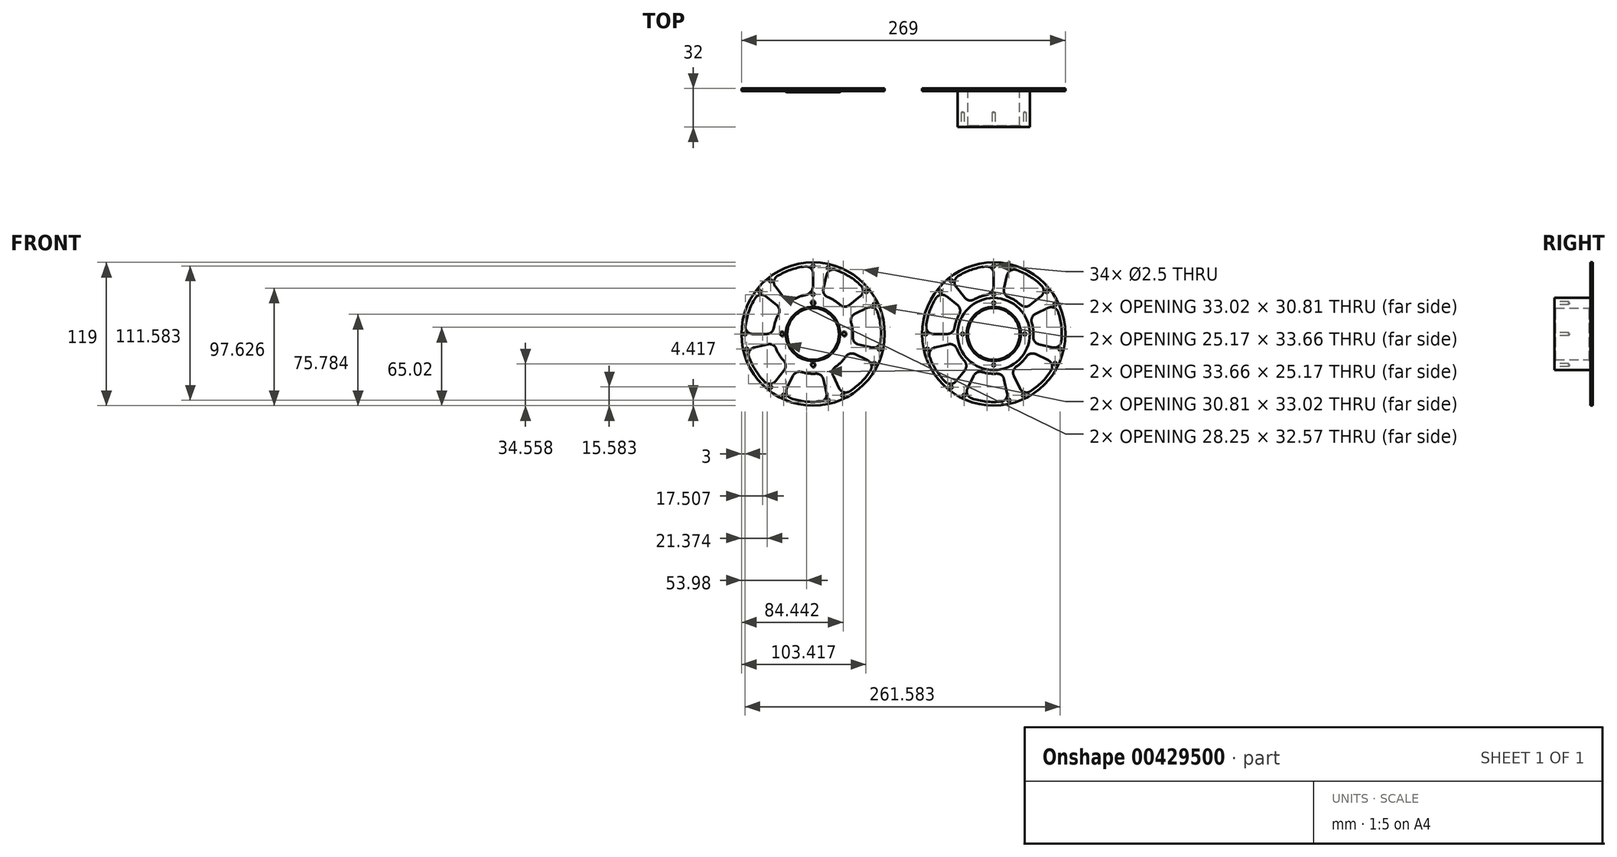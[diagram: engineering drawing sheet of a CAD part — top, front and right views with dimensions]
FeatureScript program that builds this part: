
annotation { "Feature Type Name" : "Feature", "Feature Type Description" : "" }
export const myFeature = defineFeature(function(context is Context, id is Id, definition is map)
    precondition{}
    {
        {
            var Q0;
            Q0=qCreatedBy(makeId("Front.planeOp"),FACE);
            var sketch = newSketch(context, id + "F0", { "sketchPlane" : qUnion([Q0])});
            skCircle(sketch, "E0", {"center": v(0, 0) * mm, "radius": 21.5 * mm});
            skCircle(sketch, "E1", {"center": v(0, 0) * mm, "radius": 30 * mm});
            skCircle(sketch, "E2", {"center": v(0, 0) * mm, "radius": 59.5 * mm});
            skArc(sketch, "E3", {"start": v(-6.44, 32.37) * mm, "mid": v(-11.55, 30.91) * mm, "end": v(-16.36, 28.66) * mm});
            skArc(sketch, "E4", {"start": v(-48.05, 29.73) * mm, "mid": v(-53.33, 18.66) * mm, "end": v(-56.1, 6.71) * mm});
            skLineSegment(sketch, "E5", {"start": v(0, 40.21) * mm, "end": v(0, 50.14) * mm});
            skLineSegment(sketch, "E6.1.0", {"start": v(-30.13, 24.03) * mm, "end": v(-39.2, 31.26) * mm});
            skLineSegment(sketch, "E6.2.0", {"start": v(-37.57, -8.57) * mm, "end": v(-48.89, -11.16) * mm});
            skLineSegment(sketch, "E6.3.0", {"start": v(-16.72, -34.72) * mm, "end": v(-21.76, -45.18) * mm});
            skLineSegment(sketch, "E6.4.0", {"start": v(16.72, -34.72) * mm, "end": v(21.76, -45.18) * mm});
            skLineSegment(sketch, "E6.5.0", {"start": v(37.57, -8.57) * mm, "end": v(48.89, -11.16) * mm});
            skLineSegment(sketch, "E7.1.6.0", {"start": v(30.13, 24.03) * mm, "end": v(39.2, 31.26) * mm});
            skLineSegment(sketch, "E8", {"start": v(-38.54, 0) * mm, "end": v(-50.14, 0) * mm});
            skLineSegment(sketch, "E9.1.0", {"start": v(-24.03, -30.13) * mm, "end": v(-31.26, -39.2) * mm});
            skLineSegment(sketch, "E9.2.0", {"start": v(8.57, -37.57) * mm, "end": v(11.16, -48.89) * mm});
            skLineSegment(sketch, "E9.3.0", {"start": v(34.72, -16.72) * mm, "end": v(45.18, -21.76) * mm});
            skLineSegment(sketch, "E9.4.0", {"start": v(34.72, 16.72) * mm, "end": v(45.18, 21.76) * mm});
            skLineSegment(sketch, "E9.5.0", {"start": v(8.57, 37.57) * mm, "end": v(11.16, 48.89) * mm});
            skLineSegment(sketch, "E9.6.0", {"start": v(-24.03, 30.13) * mm, "end": v(-31.26, 39.2) * mm});
            skArc(sketch, "E10.trimOffspring", {"start": v(-6.71, 56.1) * mm, "mid": v(-18.66, 53.33) * mm, "end": v(-29.73, 48.05) * mm});
            skArc(sketch, "E11.trimOffspring", {"start": v(-28.66, 16.36) * mm, "mid": v(-31.15, 10.9) * mm, "end": v(-32.6, 5.08) * mm});
            skArc(sketch, "E12.trimOffspring", {"start": v(-53.2, -19.03) * mm, "mid": v(-47.84, -30.06) * mm, "end": v(-40.23, -39.68) * mm});
            skArc(sketch, "E13.trimOffspring", {"start": v(-30.66, -12.2) * mm, "mid": v(-27.94, -17.56) * mm, "end": v(-24.3, -22.33) * mm});
            skArc(sketch, "E14.trimOffspring", {"start": v(-9.57, -31.58) * mm, "mid": v(-3.7, -32.8) * mm, "end": v(2.3, -32.92) * mm});
            skArc(sketch, "E15.trimOffspring", {"start": v(-18.3, -53.46) * mm, "mid": v(-6.33, -56.14) * mm, "end": v(5.94, -56.19) * mm});
            skArc(sketch, "E16.trimOffspring", {"start": v(18.72, -27.18) * mm, "mid": v(23.33, -23.33) * mm, "end": v(27.18, -18.72) * mm});
            skArc(sketch, "E17.trimOffspring", {"start": v(30.39, -47.63) * mm, "mid": v(39.95, -39.95) * mm, "end": v(47.63, -30.39) * mm});
            skArc(sketch, "E18.trimOffspring", {"start": v(32.92, -2.3) * mm, "mid": v(32.8, 3.7) * mm, "end": v(31.58, 9.57) * mm});
            skArc(sketch, "E19.trimOffspring", {"start": v(56.19, -5.94) * mm, "mid": v(56.14, 6.33) * mm, "end": v(53.46, 18.3) * mm});
            skArc(sketch, "E20.trimOffspring", {"start": v(39.68, 40.23) * mm, "mid": v(30.06, 47.84) * mm, "end": v(19.03, 53.2) * mm});
            skArc(sketch, "E21.trimOffspring", {"start": v(22.33, 24.3) * mm, "mid": v(17.56, 27.94) * mm, "end": v(12.2, 30.66) * mm});
            skPoint(sketch, "E22.visualSharp", {"position": v(-35.23, 44.17) * mm});
            skArc(sketch, "E22.filletArc", {"start": v(-29.73, 48.05) * mm, "mid": v(-32.48, 43.97) * mm, "end": v(-31.26, 39.2) * mm});
            skPoint(sketch, "E23.visualSharp", {"position": v(-20.58, 25.8) * mm});
            skArc(sketch, "E23.filletArc", {"start": v(-24.03, 30.13) * mm, "mid": v(-20.47, 27.98) * mm, "end": v(-16.36, 28.66) * mm});
            skPoint(sketch, "E24.visualSharp", {"position": v(0, 56.5) * mm});
            skArc(sketch, "E24.filletArc", {"start": v(0, 50.14) * mm, "mid": v(-2.02, 54.63) * mm, "end": v(-6.71, 56.1) * mm});
            skPoint(sketch, "E25.visualSharp", {"position": v(0, 33) * mm});
            skArc(sketch, "E25.filletArc", {"start": v(-6.44, 32.37) * mm, "mid": v(-1.82, 35.14) * mm, "end": v(0, 40.21) * mm});
            skPoint(sketch, "E26.visualSharp", {"position": v(12.57, 55.08) * mm});
            skArc(sketch, "E26.filletArc", {"start": v(19.03, 53.2) * mm, "mid": v(14.12, 52.81) * mm, "end": v(11.16, 48.89) * mm});
            skPoint(sketch, "E27.visualSharp", {"position": v(7.34, 32.17) * mm});
            skArc(sketch, "E27.filletArc", {"start": v(8.57, 37.57) * mm, "mid": v(9.11, 33.44) * mm, "end": v(12.2, 30.66) * mm});
            skPoint(sketch, "E28.visualSharp", {"position": v(25.8, 20.58) * mm});
            skArc(sketch, "E28.filletArc", {"start": v(22.33, 24.3) * mm, "mid": v(26.18, 22.72) * mm, "end": v(30.13, 24.03) * mm});
            skPoint(sketch, "E29.visualSharp", {"position": v(44.17, 35.23) * mm});
            skArc(sketch, "E29.filletArc", {"start": v(39.2, 31.26) * mm, "mid": v(41.45, 35.64) * mm, "end": v(39.68, 40.23) * mm});
            skPoint(sketch, "E30.visualSharp", {"position": v(50.9, 24.51) * mm});
            skArc(sketch, "E30.filletArc", {"start": v(53.46, 18.3) * mm, "mid": v(50.1, 21.89) * mm, "end": v(45.18, 21.76) * mm});
            skPoint(sketch, "E31.visualSharp", {"position": v(29.73, 14.32) * mm});
            skArc(sketch, "E31.filletArc", {"start": v(34.72, 16.72) * mm, "mid": v(31.83, 13.73) * mm, "end": v(31.58, 9.57) * mm});
            skPoint(sketch, "E32.visualSharp", {"position": v(32.17, -7.34) * mm});
            skArc(sketch, "E32.filletArc", {"start": v(32.92, -2.3) * mm, "mid": v(34.09, -6.3) * mm, "end": v(37.57, -8.57) * mm});
            skPoint(sketch, "E33.visualSharp", {"position": v(55.08, -12.57) * mm});
            skArc(sketch, "E33.filletArc", {"start": v(48.89, -11.16) * mm, "mid": v(53.7, -10.19) * mm, "end": v(56.19, -5.94) * mm});
            skPoint(sketch, "E34.visualSharp", {"position": v(29.73, -14.32) * mm});
            skArc(sketch, "E34.filletArc", {"start": v(34.72, -16.72) * mm, "mid": v(30.58, -16.33) * mm, "end": v(27.18, -18.72) * mm});
            skPoint(sketch, "E35.visualSharp", {"position": v(50.9, -24.51) * mm});
            skArc(sketch, "E35.filletArc", {"start": v(47.63, -30.39) * mm, "mid": v(48.34, -25.52) * mm, "end": v(45.18, -21.76) * mm});
            skPoint(sketch, "E36.visualSharp", {"position": v(24.51, -50.9) * mm});
            skArc(sketch, "E36.filletArc", {"start": v(21.76, -45.18) * mm, "mid": v(25.52, -48.34) * mm, "end": v(30.39, -47.63) * mm});
            skPoint(sketch, "E37.visualSharp", {"position": v(14.32, -29.73) * mm});
            skArc(sketch, "E37.filletArc", {"start": v(18.72, -27.18) * mm, "mid": v(16.33, -30.58) * mm, "end": v(16.72, -34.72) * mm});
            skPoint(sketch, "E38.visualSharp", {"position": v(7.34, -32.17) * mm});
            skArc(sketch, "E38.filletArc", {"start": v(8.57, -37.57) * mm, "mid": v(6.3, -34.09) * mm, "end": v(2.3, -32.92) * mm});
            skPoint(sketch, "E39.visualSharp", {"position": v(12.57, -55.08) * mm});
            skArc(sketch, "E39.filletArc", {"start": v(5.94, -56.19) * mm, "mid": v(10.19, -53.7) * mm, "end": v(11.16, -48.89) * mm});
            skPoint(sketch, "E40.visualSharp", {"position": v(-24.51, -50.9) * mm});
            skArc(sketch, "E40.filletArc", {"start": v(-21.76, -45.18) * mm, "mid": v(-21.89, -50.1) * mm, "end": v(-18.3, -53.46) * mm});
            skPoint(sketch, "E41.visualSharp", {"position": v(-14.32, -29.73) * mm});
            skArc(sketch, "E41.filletArc", {"start": v(-9.57, -31.58) * mm, "mid": v(-13.73, -31.83) * mm, "end": v(-16.72, -34.72) * mm});
            skPoint(sketch, "E42.visualSharp", {"position": v(-20.58, -25.8) * mm});
            skArc(sketch, "E42.filletArc", {"start": v(-24.03, -30.13) * mm, "mid": v(-22.72, -26.18) * mm, "end": v(-24.3, -22.33) * mm});
            skPoint(sketch, "E43.visualSharp", {"position": v(-35.23, -44.17) * mm});
            skArc(sketch, "E43.filletArc", {"start": v(-40.23, -39.68) * mm, "mid": v(-35.64, -41.45) * mm, "end": v(-31.26, -39.2) * mm});
            skPoint(sketch, "E44.visualSharp", {"position": v(-55.08, -12.57) * mm});
            skArc(sketch, "E44.filletArc", {"start": v(-48.89, -11.16) * mm, "mid": v(-52.81, -14.12) * mm, "end": v(-53.2, -19.03) * mm});
            skPoint(sketch, "E45.visualSharp", {"position": v(-32.17, -7.34) * mm});
            skArc(sketch, "E45.filletArc", {"start": v(-30.66, -12.2) * mm, "mid": v(-33.44, -9.11) * mm, "end": v(-37.57, -8.57) * mm});
            skPoint(sketch, "E46.visualSharp", {"position": v(-56.5, 0) * mm});
            skArc(sketch, "E46.filletArc", {"start": v(-56.1, 6.71) * mm, "mid": v(-54.63, 2.02) * mm, "end": v(-50.14, 0) * mm});
            skPoint(sketch, "E47.visualSharp", {"position": v(-33, 0) * mm});
            skArc(sketch, "E47.filletArc", {"start": v(-38.54, 0) * mm, "mid": v(-34.63, 1.44) * mm, "end": v(-32.6, 5.08) * mm});
            skPoint(sketch, "E48.visualSharp", {"position": v(-25.8, 20.58) * mm});
            skArc(sketch, "E48.filletArc", {"start": v(-28.66, 16.36) * mm, "mid": v(-27.98, 20.47) * mm, "end": v(-30.13, 24.03) * mm});
            skPoint(sketch, "E49.visualSharp", {"position": v(-44.17, 35.23) * mm});
            skArc(sketch, "E49.filletArc", {"start": v(-39.2, 31.26) * mm, "mid": v(-43.97, 32.48) * mm, "end": v(-48.05, 29.73) * mm});
            skCircle(sketch, "E50", {"center": v(0, 56.5) * mm, "radius": 1.25 * mm});
            skCircle(sketch, "E51", {"center": v(12.57, 55.08) * mm, "radius": 1.25 * mm});
            skCircle(sketch, "E52.1.0", {"center": v(-44.17, 35.23) * mm, "radius": 1.25 * mm});
            skCircle(sketch, "E52.1.1", {"center": v(-35.23, 44.17) * mm, "radius": 1.25 * mm});
            skCircle(sketch, "E52.2.0", {"center": v(-55.08, -12.57) * mm, "radius": 1.25 * mm});
            skCircle(sketch, "E52.2.1", {"center": v(-56.5, 0) * mm, "radius": 1.25 * mm});
            skCircle(sketch, "E52.3.0", {"center": v(-24.51, -50.9) * mm, "radius": 1.25 * mm});
            skCircle(sketch, "E52.3.1", {"center": v(-35.23, -44.17) * mm, "radius": 1.25 * mm});
            skCircle(sketch, "E52.4.0", {"center": v(24.51, -50.9) * mm, "radius": 1.25 * mm});
            skCircle(sketch, "E52.4.1", {"center": v(12.57, -55.08) * mm, "radius": 1.25 * mm});
            skCircle(sketch, "E52.5.0", {"center": v(55.08, -12.57) * mm, "radius": 1.25 * mm});
            skCircle(sketch, "E52.5.1", {"center": v(50.9, -24.51) * mm, "radius": 1.25 * mm});
            skCircle(sketch, "E52.6.0", {"center": v(44.17, 35.23) * mm, "radius": 1.25 * mm});
            skCircle(sketch, "E52.6.1", {"center": v(50.9, 24.51) * mm, "radius": 1.25 * mm});
            skCircle(sketch, "E53", {"center": v(0, 33) * mm, "radius": 1.25 * mm});
            skPoint(sketch, "E54", {"position": v(0, 30) * mm});
            skPoint(sketch, "E55", {"position": v(0, 21.5) * mm});
            skPoint(sketch, "E56", {"position": v(0, 25.75) * mm});
            skPoint(sketch, "E57.1.0", {"position": v(-25.75, 0) * mm});
            skPoint(sketch, "E57.2.0", {"position": v(0, -25.75) * mm});
            skPoint(sketch, "E57.3.0", {"position": v(25.75, 0) * mm});
            skCircle(sketch, "E58", {"center": v(0, 0) * mm, "radius": 22.5 * mm});
            skSolve(sketch);
        }
        {
            var Q0;
            Q0=makeQuery(id+"F0.imprint","IMPRINT",FACE,{"disambiguationData":[TD([[makeQuery(id+"F0.imprint","IMPRINT",EDGE,{"derivedFrom":sQuery(id+"F0.wireOp",EDGE,"E1")}),-1.0]])]});
            var Q1;
            Q1=makeQuery(id+"F0.imprint","IMPRINT",FACE,{"disambiguationData":[TD([[makeQuery(id+"F0.imprint","IMPRINT",EDGE,{"derivedFrom":sQuery(id+"F0.wireOp",EDGE,"E1")}),1.0]])]});
            extrude(context, id + "F1", {"entities" : qUnion([Q0, Q1]), "depth" : 2 * mm});
        }
        {
            var Q0;
            Q0=makeQuery(id+"F1.opExtrude","SWEPT_BODY",BODY,{"disambiguationData":[OSD([sQuery(id+"F0.wireOp",EDGE,"E2"),sQuery(id+"F0.wireOp",EDGE,"E3"),sQuery(id+"F0.wireOp",EDGE,"E4"),sQuery(id+"F0.wireOp",EDGE,"E5"),sQuery(id+"F0.wireOp",EDGE,"E6.1.0"),sQuery(id+"F0.wireOp",EDGE,"E6.2.0"),sQuery(id+"F0.wireOp",EDGE,"E6.3.0"),sQuery(id+"F0.wireOp",EDGE,"E6.4.0"),sQuery(id+"F0.wireOp",EDGE,"E6.5.0"),sQuery(id+"F0.wireOp",EDGE,"E7.1.6.0"),sQuery(id+"F0.wireOp",EDGE,"E8"),sQuery(id+"F0.wireOp",EDGE,"E9.1.0"),sQuery(id+"F0.wireOp",EDGE,"E9.2.0"),sQuery(id+"F0.wireOp",EDGE,"E9.3.0"),sQuery(id+"F0.wireOp",EDGE,"E9.4.0"),sQuery(id+"F0.wireOp",EDGE,"E9.5.0"),sQuery(id+"F0.wireOp",EDGE,"E9.6.0"),sQuery(id+"F0.wireOp",EDGE,"E10.trimOffspring"),sQuery(id+"F0.wireOp",EDGE,"E11.trimOffspring"),sQuery(id+"F0.wireOp",EDGE,"E12.trimOffspring"),sQuery(id+"F0.wireOp",EDGE,"E13.trimOffspring"),sQuery(id+"F0.wireOp",EDGE,"E14.trimOffspring"),sQuery(id+"F0.wireOp",EDGE,"E15.trimOffspring"),sQuery(id+"F0.wireOp",EDGE,"E16.trimOffspring"),sQuery(id+"F0.wireOp",EDGE,"E17.trimOffspring"),sQuery(id+"F0.wireOp",EDGE,"E18.trimOffspring"),sQuery(id+"F0.wireOp",EDGE,"E19.trimOffspring"),sQuery(id+"F0.wireOp",EDGE,"E20.trimOffspring"),sQuery(id+"F0.wireOp",EDGE,"E21.trimOffspring"),sQuery(id+"F0.wireOp",EDGE,"E22.filletArc"),sQuery(id+"F0.wireOp",EDGE,"E23.filletArc"),sQuery(id+"F0.wireOp",EDGE,"E24.filletArc"),sQuery(id+"F0.wireOp",EDGE,"E25.filletArc"),sQuery(id+"F0.wireOp",EDGE,"E26.filletArc"),sQuery(id+"F0.wireOp",EDGE,"E27.filletArc"),sQuery(id+"F0.wireOp",EDGE,"E28.filletArc"),sQuery(id+"F0.wireOp",EDGE,"E29.filletArc"),sQuery(id+"F0.wireOp",EDGE,"E30.filletArc"),sQuery(id+"F0.wireOp",EDGE,"E31.filletArc"),sQuery(id+"F0.wireOp",EDGE,"E32.filletArc"),sQuery(id+"F0.wireOp",EDGE,"E33.filletArc"),sQuery(id+"F0.wireOp",EDGE,"E34.filletArc"),sQuery(id+"F0.wireOp",EDGE,"E35.filletArc"),sQuery(id+"F0.wireOp",EDGE,"E36.filletArc"),sQuery(id+"F0.wireOp",EDGE,"E37.filletArc"),sQuery(id+"F0.wireOp",EDGE,"E38.filletArc"),sQuery(id+"F0.wireOp",EDGE,"E39.filletArc"),sQuery(id+"F0.wireOp",EDGE,"E40.filletArc"),sQuery(id+"F0.wireOp",EDGE,"E41.filletArc"),sQuery(id+"F0.wireOp",EDGE,"E42.filletArc"),sQuery(id+"F0.wireOp",EDGE,"E43.filletArc"),sQuery(id+"F0.wireOp",EDGE,"E44.filletArc"),sQuery(id+"F0.wireOp",EDGE,"E45.filletArc"),sQuery(id+"F0.wireOp",EDGE,"E46.filletArc"),sQuery(id+"F0.wireOp",EDGE,"E47.filletArc"),sQuery(id+"F0.wireOp",EDGE,"E48.filletArc"),sQuery(id+"F0.wireOp",EDGE,"E49.filletArc"),sQuery(id+"F0.wireOp",EDGE,"E50"),sQuery(id+"F0.wireOp",EDGE,"E51"),sQuery(id+"F0.wireOp",EDGE,"E52.1.0"),sQuery(id+"F0.wireOp",EDGE,"E52.1.1"),sQuery(id+"F0.wireOp",EDGE,"E52.2.0"),sQuery(id+"F0.wireOp",EDGE,"E52.2.1"),sQuery(id+"F0.wireOp",EDGE,"E52.3.0"),sQuery(id+"F0.wireOp",EDGE,"E52.3.1"),sQuery(id+"F0.wireOp",EDGE,"E52.4.0"),sQuery(id+"F0.wireOp",EDGE,"E52.4.1"),sQuery(id+"F0.wireOp",EDGE,"E52.5.0"),sQuery(id+"F0.wireOp",EDGE,"E52.5.1"),sQuery(id+"F0.wireOp",EDGE,"E52.6.0"),sQuery(id+"F0.wireOp",EDGE,"E52.6.1"),sQuery(id+"F0.wireOp",EDGE,"E53"),sQuery(id+"F0.wireOp",EDGE,"E58")])]});
            transform(context, id + "F2", {"entities" : qUnion([Q0]), "transformType" : TransformType.TRANSLATION_3D, "dx" : 150 * mm, "dy" : 0 * mm, "dz" : 0 * mm, "makeCopy" : true});
        }
        {
            var Q0;
            Q0=makeQuery(id+"F0.imprint","IMPRINT",FACE,{"disambiguationData":[TD([[makeQuery(id+"F0.imprint","IMPRINT",EDGE,{"derivedFrom":sQuery(id+"F0.wireOp",EDGE,"E0")}),-1.0]])]});
            extrude(context, id + "F3", {"entities" : qUnion([Q0]), "operationType" : NewBodyOperationType.ADD, "depth" : 3 * mm});
        }
        {
            var Q0;
            Q0=makeQuery(id+"F3.opExtrude","CAP_EDGE",EDGE,{"disambiguationData":[OSD([sQuery(id+"F0.wireOp",EDGE,"E58")])],"isStart":false});
            chamfer(context, id + "F4", {"entities" : qUnion([Q0]), "width" : 0.25 * mm, "tangentPropagation" : true});
        }
        {
            var Q0;
            Q0=sQuery(id+"F0.wireOp",VERTEX,"E57.3.0");
            var Q1;
            Q1=sQuery(id+"F0.wireOp",VERTEX,"E57.2.0");
            var Q2;
            Q2=sQuery(id+"F0.wireOp",VERTEX,"E57.1.0");
            var Q3;
            Q3=sQuery(id+"F0.wireOp",VERTEX,"E56");
            var Q4;
            Q4=makeQuery(id+"F1.opExtrude","SWEPT_BODY",BODY,{"disambiguationData":[OSD([sQuery(id+"F0.wireOp",EDGE,"E2"),sQuery(id+"F0.wireOp",EDGE,"E3"),sQuery(id+"F0.wireOp",EDGE,"E4"),sQuery(id+"F0.wireOp",EDGE,"E5"),sQuery(id+"F0.wireOp",EDGE,"E6.1.0"),sQuery(id+"F0.wireOp",EDGE,"E6.2.0"),sQuery(id+"F0.wireOp",EDGE,"E6.3.0"),sQuery(id+"F0.wireOp",EDGE,"E6.4.0"),sQuery(id+"F0.wireOp",EDGE,"E6.5.0"),sQuery(id+"F0.wireOp",EDGE,"E7.1.6.0"),sQuery(id+"F0.wireOp",EDGE,"E8"),sQuery(id+"F0.wireOp",EDGE,"E9.1.0"),sQuery(id+"F0.wireOp",EDGE,"E9.2.0"),sQuery(id+"F0.wireOp",EDGE,"E9.3.0"),sQuery(id+"F0.wireOp",EDGE,"E9.4.0"),sQuery(id+"F0.wireOp",EDGE,"E9.5.0"),sQuery(id+"F0.wireOp",EDGE,"E9.6.0"),sQuery(id+"F0.wireOp",EDGE,"E10.trimOffspring"),sQuery(id+"F0.wireOp",EDGE,"E11.trimOffspring"),sQuery(id+"F0.wireOp",EDGE,"E12.trimOffspring"),sQuery(id+"F0.wireOp",EDGE,"E13.trimOffspring"),sQuery(id+"F0.wireOp",EDGE,"E14.trimOffspring"),sQuery(id+"F0.wireOp",EDGE,"E15.trimOffspring"),sQuery(id+"F0.wireOp",EDGE,"E16.trimOffspring"),sQuery(id+"F0.wireOp",EDGE,"E17.trimOffspring"),sQuery(id+"F0.wireOp",EDGE,"E18.trimOffspring"),sQuery(id+"F0.wireOp",EDGE,"E19.trimOffspring"),sQuery(id+"F0.wireOp",EDGE,"E20.trimOffspring"),sQuery(id+"F0.wireOp",EDGE,"E21.trimOffspring"),sQuery(id+"F0.wireOp",EDGE,"E22.filletArc"),sQuery(id+"F0.wireOp",EDGE,"E23.filletArc"),sQuery(id+"F0.wireOp",EDGE,"E24.filletArc"),sQuery(id+"F0.wireOp",EDGE,"E25.filletArc"),sQuery(id+"F0.wireOp",EDGE,"E26.filletArc"),sQuery(id+"F0.wireOp",EDGE,"E27.filletArc"),sQuery(id+"F0.wireOp",EDGE,"E28.filletArc"),sQuery(id+"F0.wireOp",EDGE,"E29.filletArc"),sQuery(id+"F0.wireOp",EDGE,"E30.filletArc"),sQuery(id+"F0.wireOp",EDGE,"E31.filletArc"),sQuery(id+"F0.wireOp",EDGE,"E32.filletArc"),sQuery(id+"F0.wireOp",EDGE,"E33.filletArc"),sQuery(id+"F0.wireOp",EDGE,"E34.filletArc"),sQuery(id+"F0.wireOp",EDGE,"E35.filletArc"),sQuery(id+"F0.wireOp",EDGE,"E36.filletArc"),sQuery(id+"F0.wireOp",EDGE,"E37.filletArc"),sQuery(id+"F0.wireOp",EDGE,"E38.filletArc"),sQuery(id+"F0.wireOp",EDGE,"E39.filletArc"),sQuery(id+"F0.wireOp",EDGE,"E40.filletArc"),sQuery(id+"F0.wireOp",EDGE,"E41.filletArc"),sQuery(id+"F0.wireOp",EDGE,"E42.filletArc"),sQuery(id+"F0.wireOp",EDGE,"E43.filletArc"),sQuery(id+"F0.wireOp",EDGE,"E44.filletArc"),sQuery(id+"F0.wireOp",EDGE,"E45.filletArc"),sQuery(id+"F0.wireOp",EDGE,"E46.filletArc"),sQuery(id+"F0.wireOp",EDGE,"E47.filletArc"),sQuery(id+"F0.wireOp",EDGE,"E48.filletArc"),sQuery(id+"F0.wireOp",EDGE,"E49.filletArc"),sQuery(id+"F0.wireOp",EDGE,"E50"),sQuery(id+"F0.wireOp",EDGE,"E51"),sQuery(id+"F0.wireOp",EDGE,"E52.1.0"),sQuery(id+"F0.wireOp",EDGE,"E52.1.1"),sQuery(id+"F0.wireOp",EDGE,"E52.2.0"),sQuery(id+"F0.wireOp",EDGE,"E52.2.1"),sQuery(id+"F0.wireOp",EDGE,"E52.3.0"),sQuery(id+"F0.wireOp",EDGE,"E52.3.1"),sQuery(id+"F0.wireOp",EDGE,"E52.4.0"),sQuery(id+"F0.wireOp",EDGE,"E52.4.1"),sQuery(id+"F0.wireOp",EDGE,"E52.5.0"),sQuery(id+"F0.wireOp",EDGE,"E52.5.1"),sQuery(id+"F0.wireOp",EDGE,"E52.6.0"),sQuery(id+"F0.wireOp",EDGE,"E52.6.1"),sQuery(id+"F0.wireOp",EDGE,"E53"),sQuery(id+"F0.wireOp",EDGE,"E58")])]});
            hole(context, id + "F5", {"style" : HoleStyle.C_SINK, "endStyle" : HoleEndStyle.THROUGH, "oppositeDirection" : true, "holeDiameter" : 3 * mm, "cSinkDiameter" : 5 * mm, "cSinkAngle" : 90 * degree, "isTappedThrough" : true, "tappedDepth" : 12 * mm, "tapClearance" : 3, "locations" : qUnion([Q0, Q1, Q2, Q3]), "scope" : qUnion([Q4])});
        }
        {
            var Q0;
            Q0=makeQuery(id+"F2.opPattern","COPY",FACE,{"derivedFrom":makeQuery(id+"F1.opExtrude","CAP_FACE",FACE,{"disambiguationData":[OSD([sQuery(id+"F0.wireOp",EDGE,"E2"),sQuery(id+"F0.wireOp",EDGE,"E3"),sQuery(id+"F0.wireOp",EDGE,"E4"),sQuery(id+"F0.wireOp",EDGE,"E5"),sQuery(id+"F0.wireOp",EDGE,"E6.1.0"),sQuery(id+"F0.wireOp",EDGE,"E6.2.0"),sQuery(id+"F0.wireOp",EDGE,"E6.3.0"),sQuery(id+"F0.wireOp",EDGE,"E6.4.0"),sQuery(id+"F0.wireOp",EDGE,"E6.5.0"),sQuery(id+"F0.wireOp",EDGE,"E7.1.6.0"),sQuery(id+"F0.wireOp",EDGE,"E8"),sQuery(id+"F0.wireOp",EDGE,"E9.1.0"),sQuery(id+"F0.wireOp",EDGE,"E9.2.0"),sQuery(id+"F0.wireOp",EDGE,"E9.3.0"),sQuery(id+"F0.wireOp",EDGE,"E9.4.0"),sQuery(id+"F0.wireOp",EDGE,"E9.5.0"),sQuery(id+"F0.wireOp",EDGE,"E9.6.0"),sQuery(id+"F0.wireOp",EDGE,"E10.trimOffspring"),sQuery(id+"F0.wireOp",EDGE,"E11.trimOffspring"),sQuery(id+"F0.wireOp",EDGE,"E12.trimOffspring"),sQuery(id+"F0.wireOp",EDGE,"E13.trimOffspring"),sQuery(id+"F0.wireOp",EDGE,"E14.trimOffspring"),sQuery(id+"F0.wireOp",EDGE,"E15.trimOffspring"),sQuery(id+"F0.wireOp",EDGE,"E16.trimOffspring"),sQuery(id+"F0.wireOp",EDGE,"E17.trimOffspring"),sQuery(id+"F0.wireOp",EDGE,"E18.trimOffspring"),sQuery(id+"F0.wireOp",EDGE,"E19.trimOffspring"),sQuery(id+"F0.wireOp",EDGE,"E20.trimOffspring"),sQuery(id+"F0.wireOp",EDGE,"E21.trimOffspring"),sQuery(id+"F0.wireOp",EDGE,"E22.filletArc"),sQuery(id+"F0.wireOp",EDGE,"E23.filletArc"),sQuery(id+"F0.wireOp",EDGE,"E24.filletArc"),sQuery(id+"F0.wireOp",EDGE,"E25.filletArc"),sQuery(id+"F0.wireOp",EDGE,"E26.filletArc"),sQuery(id+"F0.wireOp",EDGE,"E27.filletArc"),sQuery(id+"F0.wireOp",EDGE,"E28.filletArc"),sQuery(id+"F0.wireOp",EDGE,"E29.filletArc"),sQuery(id+"F0.wireOp",EDGE,"E30.filletArc"),sQuery(id+"F0.wireOp",EDGE,"E31.filletArc"),sQuery(id+"F0.wireOp",EDGE,"E32.filletArc"),sQuery(id+"F0.wireOp",EDGE,"E33.filletArc"),sQuery(id+"F0.wireOp",EDGE,"E34.filletArc"),sQuery(id+"F0.wireOp",EDGE,"E35.filletArc"),sQuery(id+"F0.wireOp",EDGE,"E36.filletArc"),sQuery(id+"F0.wireOp",EDGE,"E37.filletArc"),sQuery(id+"F0.wireOp",EDGE,"E38.filletArc"),sQuery(id+"F0.wireOp",EDGE,"E39.filletArc"),sQuery(id+"F0.wireOp",EDGE,"E40.filletArc"),sQuery(id+"F0.wireOp",EDGE,"E41.filletArc"),sQuery(id+"F0.wireOp",EDGE,"E42.filletArc"),sQuery(id+"F0.wireOp",EDGE,"E43.filletArc"),sQuery(id+"F0.wireOp",EDGE,"E44.filletArc"),sQuery(id+"F0.wireOp",EDGE,"E45.filletArc"),sQuery(id+"F0.wireOp",EDGE,"E46.filletArc"),sQuery(id+"F0.wireOp",EDGE,"E47.filletArc"),sQuery(id+"F0.wireOp",EDGE,"E48.filletArc"),sQuery(id+"F0.wireOp",EDGE,"E49.filletArc"),sQuery(id+"F0.wireOp",EDGE,"E50"),sQuery(id+"F0.wireOp",EDGE,"E51"),sQuery(id+"F0.wireOp",EDGE,"E52.1.0"),sQuery(id+"F0.wireOp",EDGE,"E52.1.1"),sQuery(id+"F0.wireOp",EDGE,"E52.2.0"),sQuery(id+"F0.wireOp",EDGE,"E52.2.1"),sQuery(id+"F0.wireOp",EDGE,"E52.3.0"),sQuery(id+"F0.wireOp",EDGE,"E52.3.1"),sQuery(id+"F0.wireOp",EDGE,"E52.4.0"),sQuery(id+"F0.wireOp",EDGE,"E52.4.1"),sQuery(id+"F0.wireOp",EDGE,"E52.5.0"),sQuery(id+"F0.wireOp",EDGE,"E52.5.1"),sQuery(id+"F0.wireOp",EDGE,"E52.6.0"),sQuery(id+"F0.wireOp",EDGE,"E52.6.1"),sQuery(id+"F0.wireOp",EDGE,"E53"),sQuery(id+"F0.wireOp",EDGE,"E58")])],"isStart":false}),"instanceName":"1"});
            var sketch = newSketch(context, id + "F6", { "sketchPlane" : qUnion([Q0])});
            skCircle(sketch, "E59", {"center": v(150, 0) * mm, "radius": 21.5 * mm});
            skCircle(sketch, "E60", {"center": v(150, 0) * mm, "radius": 30 * mm});
            skLineSegment(sketch, "E61", {"start": v(84.04, 0) * mm, "end": v(215.9, 0) * mm, "construction": true});
            skSolve(sketch);
        }
        {
            var Q0;
            Q0=makeQuery(id+"F6.imprint","IMPRINT",FACE,{"disambiguationData":[TD([[makeQuery(id+"F6.imprint","IMPRINT",EDGE,{"derivedFrom":sQuery(id+"F6.wireOp",EDGE,"E60")}),1.0]])]});
            extrude(context, id + "F7", {"entities" : qUnion([Q0]), "operationType" : NewBodyOperationType.ADD, "depth" : 30 * mm});
        }
        {
            var Q0;
            Q0=makeQuery(id+"F6.imprint","IMPRINT",FACE,{"disambiguationData":[TD([[makeQuery(id+"F6.imprint","IMPRINT",EDGE,{"derivedFrom":sQuery(id+"F6.wireOp",EDGE,"E59")}),-1.0]])]});
            extrude(context, id + "F8", {"entities" : qUnion([Q0]), "operationType" : NewBodyOperationType.ADD, "depth" : 29 * mm, "hasSecondDirection" : true, "secondDirectionOppositeDirection" : true, "secondDirectionDepth" : 2 * mm});
        }
        {
            var Q0;
            Q0=makeQuery(id+"F7.opExtrude","CAP_FACE",FACE,{"disambiguationData":[OSD([sQuery(id+"F0.wireOp",EDGE,"E58"),sQuery(id+"F6.wireOp",EDGE,"E60")])],"isStart":false});
            var sketch = newSketch(context, id + "F9", { "sketchPlane" : qUnion([Q0])});
            skPoint(sketch, "E62", {"position": v(180, 0) * mm});
            skPoint(sketch, "E63", {"position": v(175.75, 0) * mm});
            skPoint(sketch, "E64", {"position": v(171.5, 0) * mm});
            skPoint(sketch, "E65", {"position": v(128.5, 0) * mm});
            skPoint(sketch, "E66", {"position": v(124.25, 0) * mm});
            skPoint(sketch, "E67", {"position": v(120, 0) * mm});
            skLineSegment(sketch, "E68", {"start": v(150, 73.8) * mm, "end": v(150, -73.8) * mm, "construction": true});
            skPoint(sketch, "E69", {"position": v(150, 30) * mm});
            skPoint(sketch, "E70", {"position": v(150, 21.5) * mm});
            skPoint(sketch, "E71", {"position": v(150, 25.75) * mm});
            skPoint(sketch, "E72", {"position": v(150, -21.5) * mm});
            skPoint(sketch, "E73", {"position": v(150, -30) * mm});
            skPoint(sketch, "E74", {"position": v(150, -25.75) * mm});
            skSolve(sketch);
        }
        {
            var Q0;
            Q0=sQuery(id+"F9.wireOp",VERTEX,"E63");
            var Q1;
            Q1=sQuery(id+"F9.wireOp",VERTEX,"E66");
            var Q2;
            Q2=sQuery(id+"F9.wireOp",VERTEX,"E71");
            var Q3;
            Q3=sQuery(id+"F9.wireOp",VERTEX,"E74");
            var Q4;
            Q4=makeQuery(id+"F2.opPattern","COPY",BODY,{"derivedFrom":makeQuery(id+"F1.opExtrude","SWEPT_BODY",BODY,{"disambiguationData":[OSD([sQuery(id+"F0.wireOp",EDGE,"E2"),sQuery(id+"F0.wireOp",EDGE,"E3"),sQuery(id+"F0.wireOp",EDGE,"E4"),sQuery(id+"F0.wireOp",EDGE,"E5"),sQuery(id+"F0.wireOp",EDGE,"E6.1.0"),sQuery(id+"F0.wireOp",EDGE,"E6.2.0"),sQuery(id+"F0.wireOp",EDGE,"E6.3.0"),sQuery(id+"F0.wireOp",EDGE,"E6.4.0"),sQuery(id+"F0.wireOp",EDGE,"E6.5.0"),sQuery(id+"F0.wireOp",EDGE,"E7.1.6.0"),sQuery(id+"F0.wireOp",EDGE,"E8"),sQuery(id+"F0.wireOp",EDGE,"E9.1.0"),sQuery(id+"F0.wireOp",EDGE,"E9.2.0"),sQuery(id+"F0.wireOp",EDGE,"E9.3.0"),sQuery(id+"F0.wireOp",EDGE,"E9.4.0"),sQuery(id+"F0.wireOp",EDGE,"E9.5.0"),sQuery(id+"F0.wireOp",EDGE,"E9.6.0"),sQuery(id+"F0.wireOp",EDGE,"E10.trimOffspring"),sQuery(id+"F0.wireOp",EDGE,"E11.trimOffspring"),sQuery(id+"F0.wireOp",EDGE,"E12.trimOffspring"),sQuery(id+"F0.wireOp",EDGE,"E13.trimOffspring"),sQuery(id+"F0.wireOp",EDGE,"E14.trimOffspring"),sQuery(id+"F0.wireOp",EDGE,"E15.trimOffspring"),sQuery(id+"F0.wireOp",EDGE,"E16.trimOffspring"),sQuery(id+"F0.wireOp",EDGE,"E17.trimOffspring"),sQuery(id+"F0.wireOp",EDGE,"E18.trimOffspring"),sQuery(id+"F0.wireOp",EDGE,"E19.trimOffspring"),sQuery(id+"F0.wireOp",EDGE,"E20.trimOffspring"),sQuery(id+"F0.wireOp",EDGE,"E21.trimOffspring"),sQuery(id+"F0.wireOp",EDGE,"E22.filletArc"),sQuery(id+"F0.wireOp",EDGE,"E23.filletArc"),sQuery(id+"F0.wireOp",EDGE,"E24.filletArc"),sQuery(id+"F0.wireOp",EDGE,"E25.filletArc"),sQuery(id+"F0.wireOp",EDGE,"E26.filletArc"),sQuery(id+"F0.wireOp",EDGE,"E27.filletArc"),sQuery(id+"F0.wireOp",EDGE,"E28.filletArc"),sQuery(id+"F0.wireOp",EDGE,"E29.filletArc"),sQuery(id+"F0.wireOp",EDGE,"E30.filletArc"),sQuery(id+"F0.wireOp",EDGE,"E31.filletArc"),sQuery(id+"F0.wireOp",EDGE,"E32.filletArc"),sQuery(id+"F0.wireOp",EDGE,"E33.filletArc"),sQuery(id+"F0.wireOp",EDGE,"E34.filletArc"),sQuery(id+"F0.wireOp",EDGE,"E35.filletArc"),sQuery(id+"F0.wireOp",EDGE,"E36.filletArc"),sQuery(id+"F0.wireOp",EDGE,"E37.filletArc"),sQuery(id+"F0.wireOp",EDGE,"E38.filletArc"),sQuery(id+"F0.wireOp",EDGE,"E39.filletArc"),sQuery(id+"F0.wireOp",EDGE,"E40.filletArc"),sQuery(id+"F0.wireOp",EDGE,"E41.filletArc"),sQuery(id+"F0.wireOp",EDGE,"E42.filletArc"),sQuery(id+"F0.wireOp",EDGE,"E43.filletArc"),sQuery(id+"F0.wireOp",EDGE,"E44.filletArc"),sQuery(id+"F0.wireOp",EDGE,"E45.filletArc"),sQuery(id+"F0.wireOp",EDGE,"E46.filletArc"),sQuery(id+"F0.wireOp",EDGE,"E47.filletArc"),sQuery(id+"F0.wireOp",EDGE,"E48.filletArc"),sQuery(id+"F0.wireOp",EDGE,"E49.filletArc"),sQuery(id+"F0.wireOp",EDGE,"E50"),sQuery(id+"F0.wireOp",EDGE,"E51"),sQuery(id+"F0.wireOp",EDGE,"E52.1.0"),sQuery(id+"F0.wireOp",EDGE,"E52.1.1"),sQuery(id+"F0.wireOp",EDGE,"E52.2.0"),sQuery(id+"F0.wireOp",EDGE,"E52.2.1"),sQuery(id+"F0.wireOp",EDGE,"E52.3.0"),sQuery(id+"F0.wireOp",EDGE,"E52.3.1"),sQuery(id+"F0.wireOp",EDGE,"E52.4.0"),sQuery(id+"F0.wireOp",EDGE,"E52.4.1"),sQuery(id+"F0.wireOp",EDGE,"E52.5.0"),sQuery(id+"F0.wireOp",EDGE,"E52.5.1"),sQuery(id+"F0.wireOp",EDGE,"E52.6.0"),sQuery(id+"F0.wireOp",EDGE,"E52.6.1"),sQuery(id+"F0.wireOp",EDGE,"E53"),sQuery(id+"F0.wireOp",EDGE,"E58")])]}),"instanceName":"1"});
            hole(context, id + "F10", {"style" : HoleStyle.SIMPLE, "endStyle" : HoleEndStyle.BLIND, "holeDiameter" : 2.5 * mm, "holeDepth" : 12 * mm, "isTappedThrough" : true, "tappedDepth" : 12 * mm, "tapClearance" : 3, "startFromSketch" : true, "locations" : qUnion([Q0, Q1, Q2, Q3]), "scope" : qUnion([Q4])});
        }
    });
